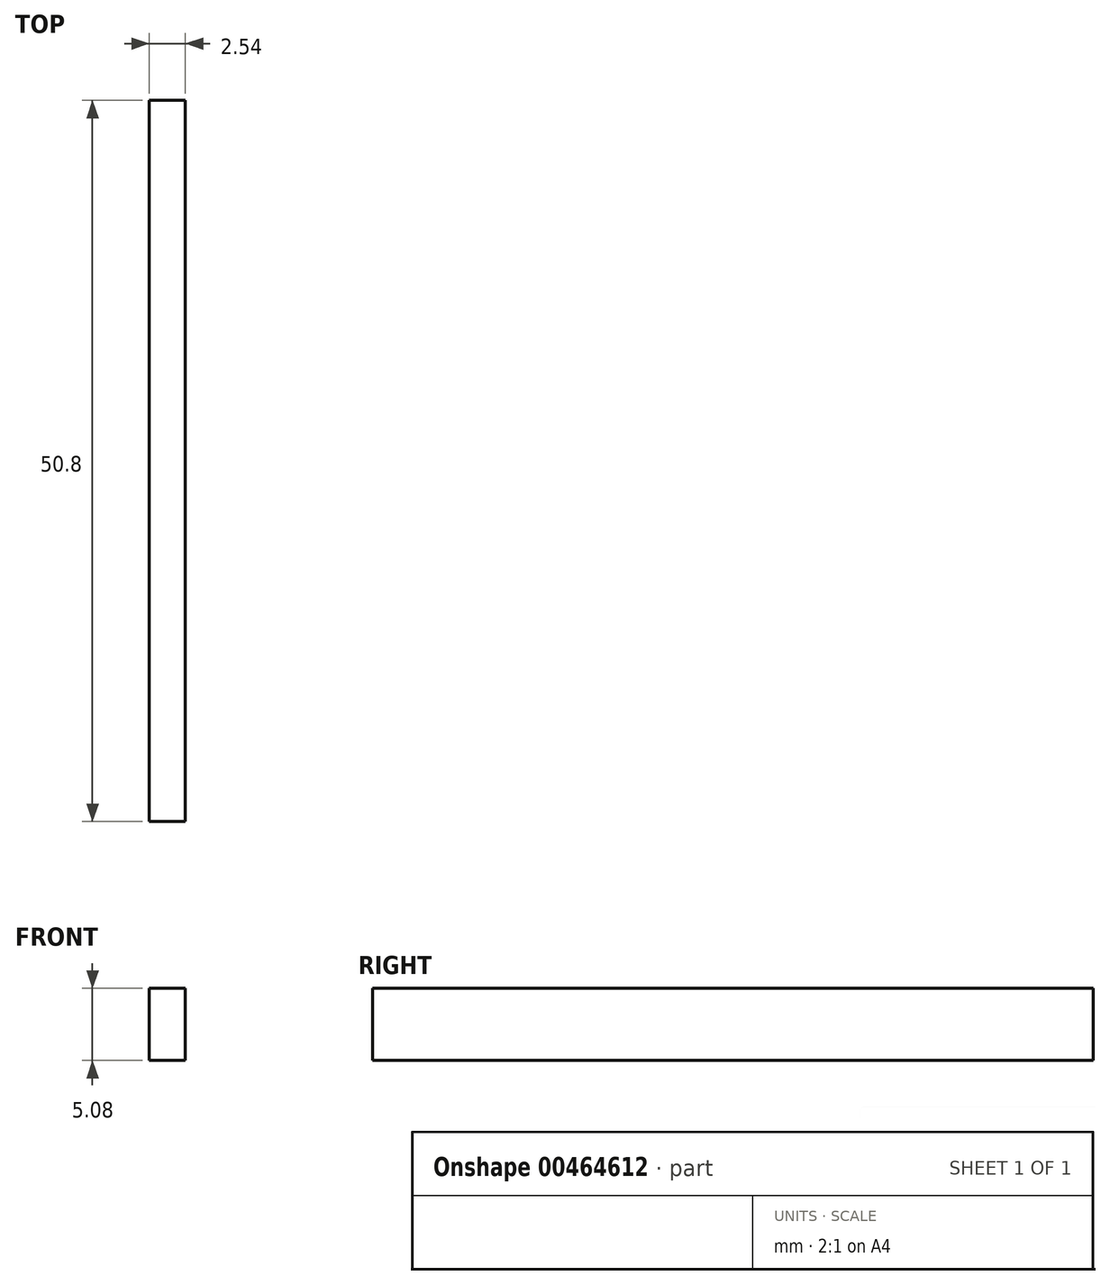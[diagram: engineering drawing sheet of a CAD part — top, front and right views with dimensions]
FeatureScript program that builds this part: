
annotation { "Feature Type Name" : "Feature", "Feature Type Description" : "" }
export const myFeature = defineFeature(function(context is Context, id is Id, definition is map)
    precondition{}
    {
        {
            var Q0;
            Q0=qCreatedBy(makeId("Top.planeOp"),FACE);
            var sketch = newSketch(context, id + "F0", { "sketchPlane" : qUnion([Q0])});
            skLineSegment(sketch, "E0.bottom", {"start": v(-33.28, 31.43) * mm, "end": v(-30.74, 31.43) * mm});
            skLineSegment(sketch, "E0.top", {"start": v(-33.28, -19.37) * mm, "end": v(-30.74, -19.37) * mm});
            skLineSegment(sketch, "E0.left", {"start": v(-33.28, 31.43) * mm, "end": v(-33.28, -19.37) * mm});
            skLineSegment(sketch, "E0.right", {"start": v(-30.74, 31.43) * mm, "end": v(-30.74, -19.37) * mm});
            skSolve(sketch);
        }
        {
            var Q0;
            Q0=makeQuery(id+"F0.imprint","IMPRINT",FACE,{"disambiguationData":[TD([[makeQuery(id+"F0.imprint","IMPRINT",EDGE,{"derivedFrom":sQuery(id+"F0.wireOp",EDGE,"E0.bottom")}),-1.0]])]});
            extrude(context, id + "F1", {"entities" : qUnion([Q0]), "depth" : 5.08 * mm});
        }
    });
